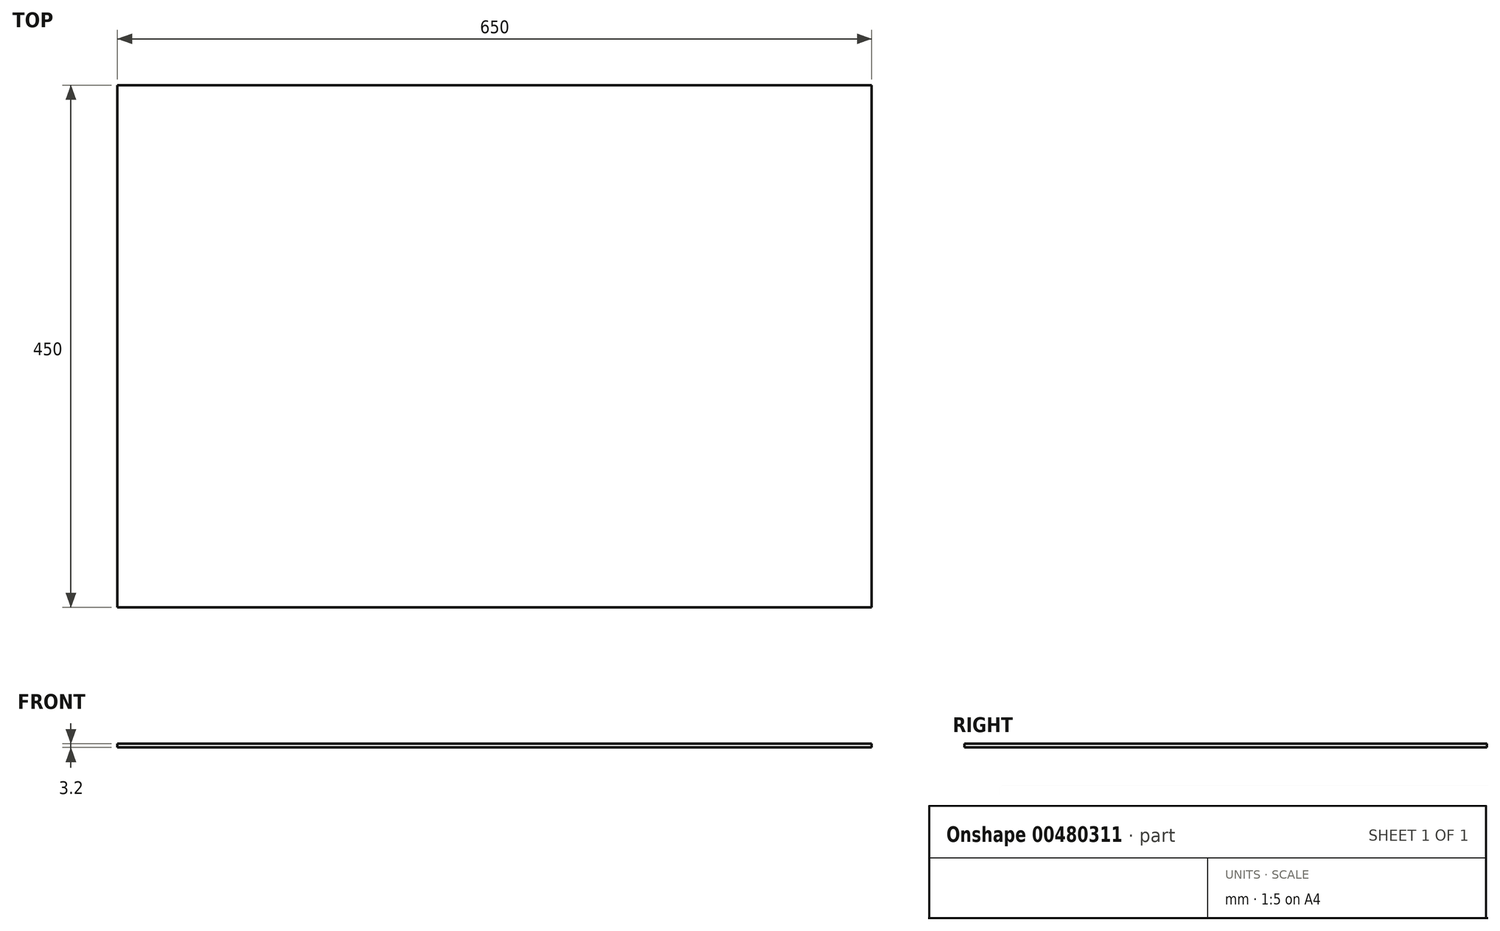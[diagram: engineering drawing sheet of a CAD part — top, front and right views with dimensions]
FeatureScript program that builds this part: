
annotation { "Feature Type Name" : "Feature", "Feature Type Description" : "" }
export const myFeature = defineFeature(function(context is Context, id is Id, definition is map)
    precondition{}
    {
        {
            var Q0;
            Q0=qCreatedBy(makeId("Top.planeOp"),FACE);
            var sketch = newSketch(context, id + "F0", { "sketchPlane" : qUnion([Q0])});
            skLineSegment(sketch, "E0.bottom", {"start": v(-325, 225) * mm, "end": v(325, 225) * mm});
            skLineSegment(sketch, "E0.top", {"start": v(-325, -225) * mm, "end": v(325, -225) * mm});
            skLineSegment(sketch, "E0.left", {"start": v(-325, 225) * mm, "end": v(-325, -225) * mm});
            skLineSegment(sketch, "E0.right", {"start": v(325, 225) * mm, "end": v(325, -225) * mm});
            skPoint(sketch, "E0.middle", {"position": v(0, 0) * mm});
            skSolve(sketch);
        }
        {
            var Q0;
            Q0=makeQuery(id+"F0.imprint","IMPRINT",FACE,{"disambiguationData":[TD([[makeQuery(id+"F0.imprint","IMPRINT",EDGE,{"derivedFrom":sQuery(id+"F0.wireOp",EDGE,"E0.bottom")}),-1.0]])]});
            extrude(context, id + "F1", {"entities" : qUnion([Q0]), "depth" : 3.2 * mm, "offsetDistance" : 25 * mm});
        }
    });
